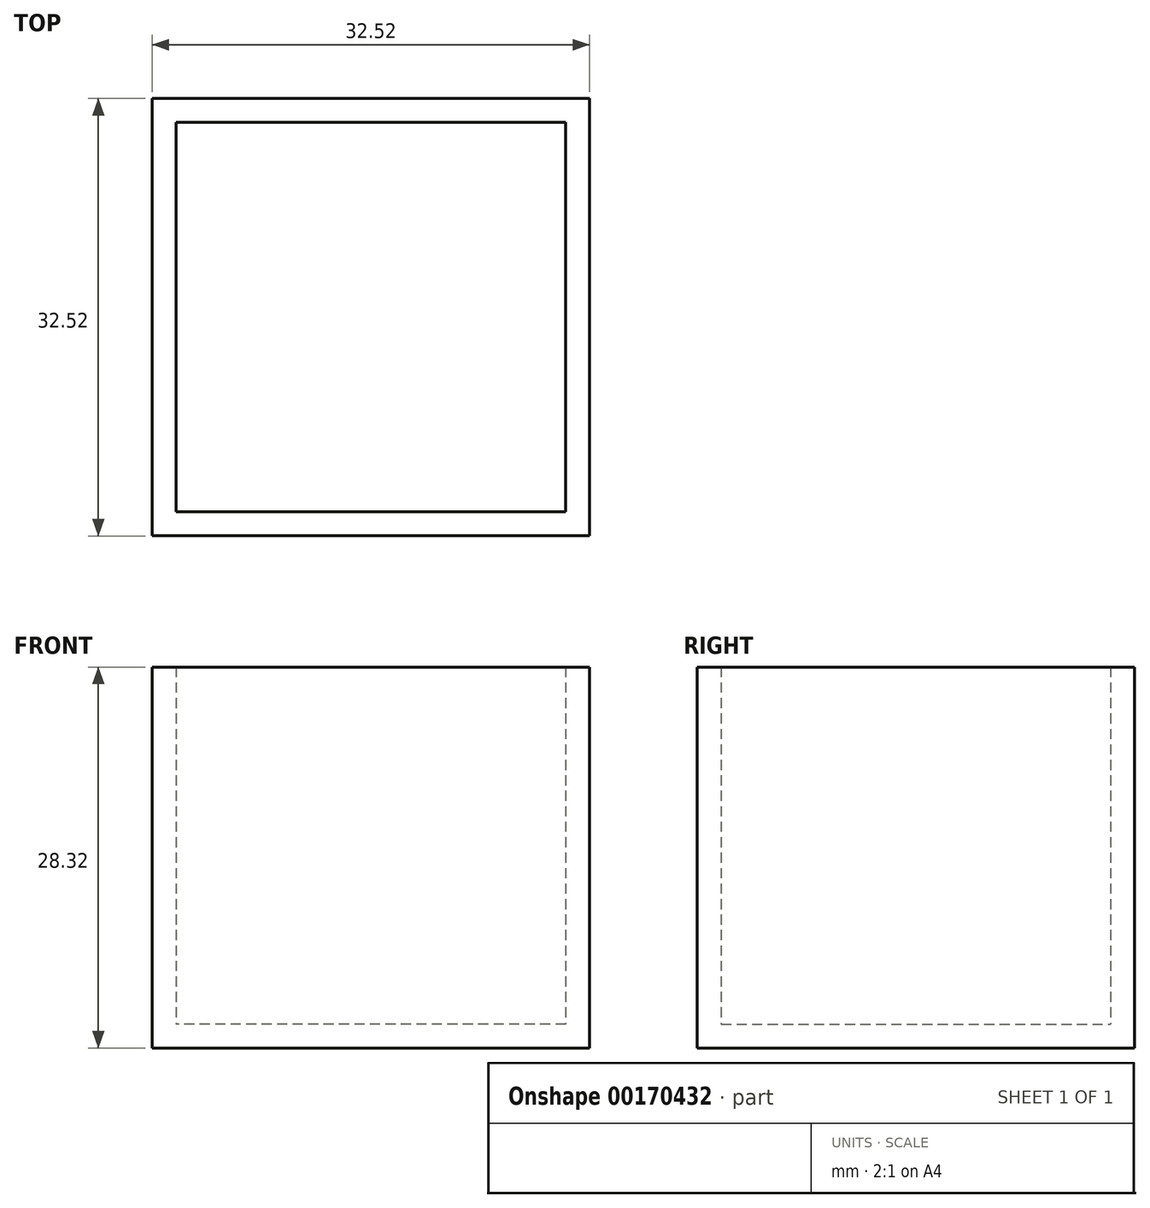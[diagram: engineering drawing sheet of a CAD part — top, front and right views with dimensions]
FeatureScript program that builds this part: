
annotation { "Feature Type Name" : "Feature", "Feature Type Description" : "" }
export const myFeature = defineFeature(function(context is Context, id is Id, definition is map)
    precondition{}
    {
        {
            var Q0;
            Q0=qCreatedBy(makeId("Top.planeOp"),FACE);
            var sketch = newSketch(context, id + "F0", { "sketchPlane" : qUnion([Q0])});
            skLineSegment(sketch, "E0.bottom", {"start": v(16.26, -16.26) * mm, "end": v(-16.26, -16.26) * mm});
            skLineSegment(sketch, "E0.top", {"start": v(16.26, 16.26) * mm, "end": v(-16.26, 16.26) * mm});
            skLineSegment(sketch, "E0.left", {"start": v(16.26, -16.26) * mm, "end": v(16.26, 16.26) * mm});
            skLineSegment(sketch, "E0.right", {"start": v(-16.26, -16.26) * mm, "end": v(-16.26, 16.26) * mm});
            skPoint(sketch, "E0.middle", {"position": v(0, 0) * mm});
            skSolve(sketch);
        }
        {
            var Q0;
            Q0=makeQuery(id+"F0.imprint","IMPRINT",FACE,{"disambiguationData":[TD([[makeQuery(id+"F0.imprint","IMPRINT",EDGE,{"derivedFrom":sQuery(id+"F0.wireOp",EDGE,"E0.bottom")}),-1.0]])]});
            extrude(context, id + "F1", {"entities" : qUnion([Q0]), "depth" : 28.32 * mm});
        }
        {
            var Q0;
            Q0=makeQuery(id+"F1.opExtrude","CAP_FACE",FACE,{"disambiguationData":[OSD([sQuery(id+"F0.wireOp",EDGE,"E0.bottom"),sQuery(id+"F0.wireOp",EDGE,"E0.top"),sQuery(id+"F0.wireOp",EDGE,"E0.left"),sQuery(id+"F0.wireOp",EDGE,"E0.right")])],"isStart":false});
            shell(context, id + "F2", {"entities" : qUnion([Q0]), "thickness" : 1.78 * mm});
        }
    });
